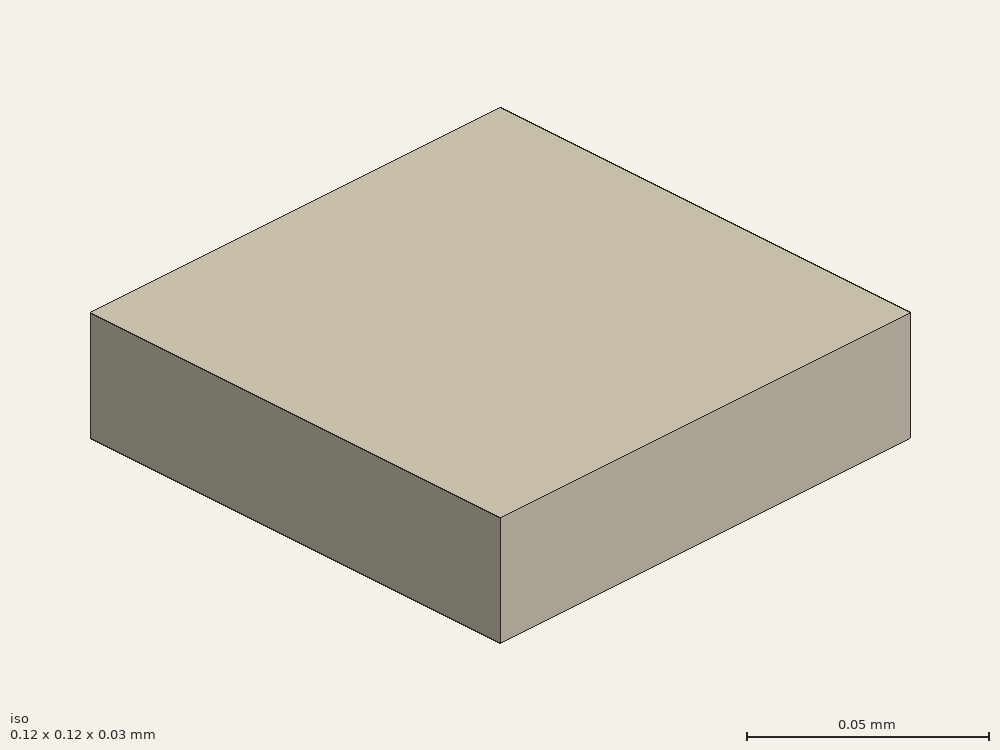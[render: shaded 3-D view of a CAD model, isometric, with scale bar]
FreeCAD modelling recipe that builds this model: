
FCSTD DOCUMENT  (FreeCAD 0.15R4671 (Git))
Label: quadrangle0
License: All rights reserved
LicenseURL: http://en.wikipedia.org/wiki/All_rights_reserved
objects: Sketcher::SketchObject×1, PartDesign::Pad×1
note: 3 computed .brp shape members not serialized (recipe doc carries the construction recipe); baked Part::Feature solids carry a one-line shape summary decoded from their .brp

FEATURE [Sketcher::SketchObject] Sketch
  sketch-geometry (4):
    g0: LineSegment StartX=0.06 StartY=0.06 StartZ=0 EndX=-0.06 EndY=0.06 EndZ=0
    g1: LineSegment StartX=-0.06 StartY=0.06 StartZ=0 EndX=-0.06 EndY=-0.06 EndZ=0
    g2: LineSegment StartX=-0.06 StartY=-0.06 StartZ=0 EndX=0.06 EndY=-0.06 EndZ=0
    g3: LineSegment StartX=0.06 StartY=-0.06 StartZ=0 EndX=0.06 EndY=0.06 EndZ=0
  constraints (13):
    c: Coincident(g0,g1)
    c: Coincident(g1,g2)
    c: Coincident(g2,g3)
    c: Coincident(g3,g0)
    c: Horizontal(g0)
    c: Horizontal(g2)
    c: Vertical(g1)
    c: Vertical(g3)
    c: Symmetric(g0,g2,g-1)
    c: Equal(g0,g2)
    c: Equal(g3,g1)
    c: DistanceY(g0,g1) = -0.12
    c: DistanceX(g0,g0) = 0.12
FEATURE [PartDesign::Pad] Pad
  Length = 0.03
  Length2 = 100
  Midplane = true
  Reversed = true
  Sketch = -> Sketch
  Type = 0
